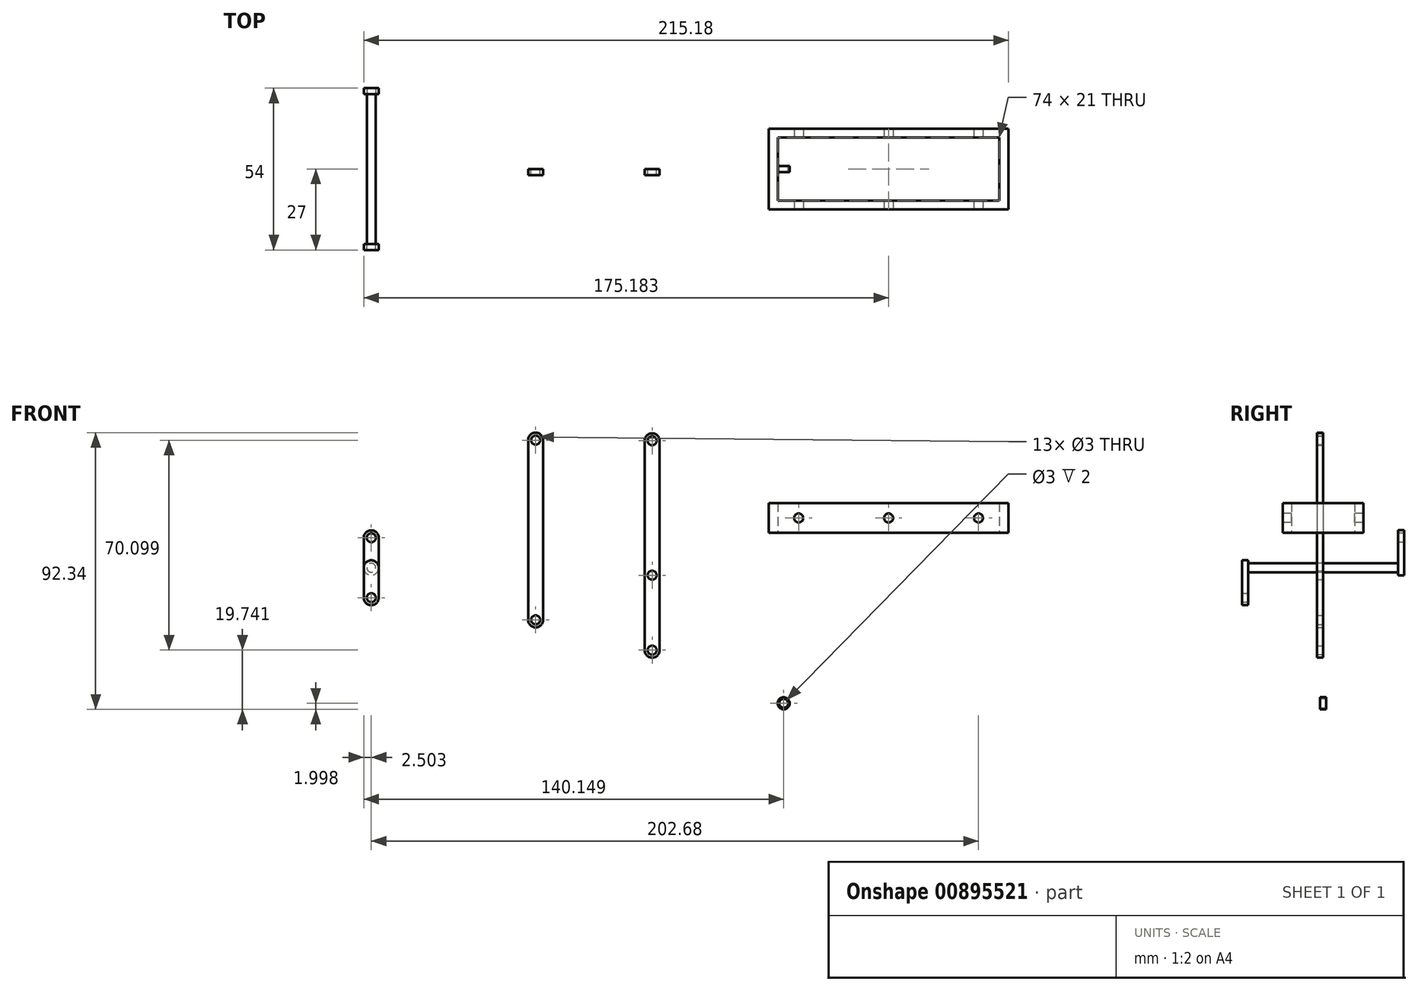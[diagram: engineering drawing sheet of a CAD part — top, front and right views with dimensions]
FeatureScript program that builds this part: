
annotation { "Feature Type Name" : "Feature", "Feature Type Description" : "" }
export const myFeature = defineFeature(function(context is Context, id is Id, definition is map)
    precondition{}
    {
        {
            var Q0;
            Q0=qCreatedBy(makeId("Front.planeOp"),FACE);
            var sketch = newSketch(context, id + "F0", { "sketchPlane" : qUnion([Q0])});
            skLineSegment(sketch, "E0.bottom", {"start": v(-57.36, 17.4) * mm, "end": v(-52.36, 17.4) * mm});
            skLineSegment(sketch, "E0.top", {"start": v(-57.36, -2.6) * mm, "end": v(-52.36, -2.6) * mm});
            skLineSegment(sketch, "E0.left", {"start": v(-57.36, 17.4) * mm, "end": v(-57.36, -2.6) * mm});
            skLineSegment(sketch, "E0.right", {"start": v(-52.36, 17.4) * mm, "end": v(-52.36, -2.6) * mm});
            skArc(sketch, "E1", {"start": v(-52.36, 17.4) * mm, "mid": v(-54.86, 19.9) * mm, "end": v(-57.36, 17.4) * mm});
            skArc(sketch, "E2", {"start": v(-57.36, -2.6) * mm, "mid": v(-54.86, -5.1) * mm, "end": v(-52.36, -2.6) * mm});
            skCircle(sketch, "E3", {"center": v(-54.86, -2.6) * mm, "radius": 1.5 * mm});
            skCircle(sketch, "E4", {"center": v(-54.86, 17.4) * mm, "radius": 1.5 * mm});
            skLineSegment(sketch, "E5", {"start": v(-57.36, 7.4) * mm, "end": v(-52.36, 7.4) * mm});
            skCircle(sketch, "E6", {"center": v(-54.86, 7.4) * mm, "radius": 2.5 * mm});
            skCircle(sketch, "E7", {"center": v(-54.86, 7.4) * mm, "radius": 1.5 * mm});
            skSolve(sketch);
        }
        {
            var Q0;
            {var subQ1=sQuery(id+"F0.wireOp",EDGE,"E5");var subQ3=sQuery(id+"F0.wireOp",EDGE,"E7");var subQ4=makeQuery(id+"F0.imprint","INTERSECT",VERTEX,{"disambiguationData":[OD(0.0)],"derivedFrom":[subQ1,subQ3]});Q0=makeQuery(id+"F0.imprint","IMPRINT",FACE,{"disambiguationData":[TD([[makeQuery(id+"F0.imprint","IMPRINT",EDGE,{"disambiguationData":[TD([[subQ4,-1.0]])],"derivedFrom":subQ3}),-1.0]])]});}
            var Q1;
            {var subQ0=sQuery(id+"F0.wireOp",EDGE,"E7");var subQ1=sQuery(id+"F0.wireOp",EDGE,"E5");var subQ2=makeQuery(id+"F0.imprint","INTERSECT",VERTEX,{"disambiguationData":[OD(0.0)],"derivedFrom":[subQ1,subQ0]});Q1=makeQuery(id+"F0.imprint","IMPRINT",FACE,{"disambiguationData":[TD([[makeQuery(id+"F0.imprint","IMPRINT",EDGE,{"disambiguationData":[TD([[subQ2,-1.0]])],"derivedFrom":subQ1}),-1.0]])]});}
            var Q2;
            {var subQ0=sQuery(id+"F0.wireOp",EDGE,"E7");var subQ1=sQuery(id+"F0.wireOp",EDGE,"E5");var subQ2=makeQuery(id+"F0.imprint","INTERSECT",VERTEX,{"disambiguationData":[OD(0.0)],"derivedFrom":[subQ1,subQ0]});Q2=makeQuery(id+"F0.imprint","IMPRINT",FACE,{"disambiguationData":[TD([[makeQuery(id+"F0.imprint","IMPRINT",EDGE,{"disambiguationData":[TD([[subQ2,-1.0]])],"derivedFrom":subQ1}),1.0]])]});}
            var Q3;
            {var subQ1=sQuery(id+"F0.wireOp",EDGE,"E5");var subQ3=sQuery(id+"F0.wireOp",EDGE,"E7");var subQ4=makeQuery(id+"F0.imprint","INTERSECT",VERTEX,{"disambiguationData":[OD(0.0)],"derivedFrom":[subQ1,subQ3]});Q3=makeQuery(id+"F0.imprint","IMPRINT",FACE,{"disambiguationData":[TD([[makeQuery(id+"F0.imprint","IMPRINT",EDGE,{"disambiguationData":[TD([[subQ4,1.0]])],"derivedFrom":subQ3}),-1.0]])]});}
            var Q4;
            {var subQ2=sQuery(id+"F0.wireOp",EDGE,"E0.bottom");var subQ10=sQuery(id+"F0.wireOp",EDGE,"E4");var subQ12=makeQuery(id+"F0.imprint","INTERSECT",VERTEX,{"disambiguationData":[OD(0.0)],"derivedFrom":[subQ2,subQ10]});Q4=makeQuery(id+"F0.imprint","IMPRINT",FACE,{"disambiguationData":[TD([[makeQuery(id+"F0.imprint","IMPRINT",EDGE,{"disambiguationData":[TD([[subQ12,-1.0]])],"derivedFrom":subQ10}),-1.0]])]});}
            var Q5;
            {var subQ0=sQuery(id+"F0.wireOp",EDGE,"E4");var subQ1=sQuery(id+"F0.wireOp",EDGE,"E0.bottom");var subQ2=makeQuery(id+"F0.imprint","INTERSECT",VERTEX,{"disambiguationData":[OD(0.0)],"derivedFrom":[subQ1,subQ0]});Q5=makeQuery(id+"F0.imprint","IMPRINT",FACE,{"disambiguationData":[TD([[makeQuery(id+"F0.imprint","IMPRINT",EDGE,{"disambiguationData":[TD([[subQ2,-1.0]])],"derivedFrom":subQ1}),-1.0]])]});}
            var Q6;
            {var subQ0=sQuery(id+"F0.wireOp",EDGE,"E4");var subQ1=sQuery(id+"F0.wireOp",EDGE,"E0.bottom");var subQ2=makeQuery(id+"F0.imprint","INTERSECT",VERTEX,{"disambiguationData":[OD(0.0)],"derivedFrom":[subQ1,subQ0]});Q6=makeQuery(id+"F0.imprint","IMPRINT",FACE,{"disambiguationData":[TD([[makeQuery(id+"F0.imprint","IMPRINT",EDGE,{"disambiguationData":[TD([[subQ2,-1.0]])],"derivedFrom":subQ1}),1.0]])]});}
            var Q7;
            {var subQ0=sQuery(id+"F0.wireOp",EDGE,"E1");Q7=makeQuery(id+"F0.imprint","IMPRINT",FACE,{"disambiguationData":[TD([[makeQuery(id+"F0.imprint","IMPRINT",EDGE,{"derivedFrom":subQ0}),1.0]])]});}
            extrude(context, id + "F1", {"entities" : qUnion([Q0, Q1, Q2, Q3, Q4, Q5, Q6, Q7]), "oppositeDirection" : true, "depth" : 27 * mm, "offsetDistance" : 25 * mm});
        }
        {
            var Q0;
            {var subQ1=sQuery(id+"F0.wireOp",EDGE,"E5");var subQ3=sQuery(id+"F0.wireOp",EDGE,"E7");var subQ4=makeQuery(id+"F0.imprint","INTERSECT",VERTEX,{"disambiguationData":[OD(0.0)],"derivedFrom":[subQ1,subQ3]});Q0=makeQuery(id+"F0.imprint","IMPRINT",FACE,{"disambiguationData":[TD([[makeQuery(id+"F0.imprint","IMPRINT",EDGE,{"disambiguationData":[TD([[subQ4,1.0]])],"derivedFrom":subQ3}),-1.0]])]});}
            var Q1;
            {var subQ0=sQuery(id+"F0.wireOp",EDGE,"E7");var subQ1=sQuery(id+"F0.wireOp",EDGE,"E5");var subQ2=makeQuery(id+"F0.imprint","INTERSECT",VERTEX,{"disambiguationData":[OD(0.0)],"derivedFrom":[subQ1,subQ0]});Q1=makeQuery(id+"F0.imprint","IMPRINT",FACE,{"disambiguationData":[TD([[makeQuery(id+"F0.imprint","IMPRINT",EDGE,{"disambiguationData":[TD([[subQ2,-1.0]])],"derivedFrom":subQ1}),1.0]])]});}
            var Q2;
            {var subQ0=sQuery(id+"F0.wireOp",EDGE,"E7");var subQ1=sQuery(id+"F0.wireOp",EDGE,"E5");var subQ2=makeQuery(id+"F0.imprint","INTERSECT",VERTEX,{"disambiguationData":[OD(0.0)],"derivedFrom":[subQ1,subQ0]});Q2=makeQuery(id+"F0.imprint","IMPRINT",FACE,{"disambiguationData":[TD([[makeQuery(id+"F0.imprint","IMPRINT",EDGE,{"disambiguationData":[TD([[subQ2,-1.0]])],"derivedFrom":subQ1}),-1.0]])]});}
            var Q3;
            {var subQ1=sQuery(id+"F0.wireOp",EDGE,"E5");var subQ3=sQuery(id+"F0.wireOp",EDGE,"E7");var subQ4=makeQuery(id+"F0.imprint","INTERSECT",VERTEX,{"disambiguationData":[OD(0.0)],"derivedFrom":[subQ1,subQ3]});Q3=makeQuery(id+"F0.imprint","IMPRINT",FACE,{"disambiguationData":[TD([[makeQuery(id+"F0.imprint","IMPRINT",EDGE,{"disambiguationData":[TD([[subQ4,-1.0]])],"derivedFrom":subQ3}),-1.0]])]});}
            var Q4;
            {var subQ2=sQuery(id+"F0.wireOp",EDGE,"E0.top");var subQ10=sQuery(id+"F0.wireOp",EDGE,"E3");var subQ12=makeQuery(id+"F0.imprint","INTERSECT",VERTEX,{"disambiguationData":[OD(0.0)],"derivedFrom":[subQ2,subQ10]});Q4=makeQuery(id+"F0.imprint","IMPRINT",FACE,{"disambiguationData":[TD([[makeQuery(id+"F0.imprint","IMPRINT",EDGE,{"disambiguationData":[TD([[subQ12,1.0]])],"derivedFrom":subQ10}),-1.0]])]});}
            var Q5;
            {var subQ0=sQuery(id+"F0.wireOp",EDGE,"E2");Q5=makeQuery(id+"F0.imprint","IMPRINT",FACE,{"disambiguationData":[TD([[makeQuery(id+"F0.imprint","IMPRINT",EDGE,{"derivedFrom":subQ0}),1.0]])]});}
            extrude(context, id + "F2", {"entities" : qUnion([Q0, Q1, Q2, Q3, Q4, Q5]), "operationType" : NewBodyOperationType.ADD, "depth" : 27 * mm, "offsetDistance" : 25 * mm});
        }
        {
            var Q0;
            {var subQ0=sQuery(id+"F0.wireOp",EDGE,"E4");var subQ1=sQuery(id+"F0.wireOp",EDGE,"E0.bottom");var subQ2=makeQuery(id+"F0.imprint","INTERSECT",VERTEX,{"disambiguationData":[OD(0.0)],"derivedFrom":[subQ1,subQ0]});Q0=makeQuery(id+"F0.imprint","IMPRINT",FACE,{"disambiguationData":[TD([[makeQuery(id+"F0.imprint","IMPRINT",EDGE,{"disambiguationData":[TD([[subQ2,-1.0]])],"derivedFrom":subQ1}),1.0]])]});}
            var Q1;
            {var subQ0=sQuery(id+"F0.wireOp",EDGE,"E4");var subQ1=sQuery(id+"F0.wireOp",EDGE,"E0.bottom");var subQ2=makeQuery(id+"F0.imprint","INTERSECT",VERTEX,{"disambiguationData":[OD(0.0)],"derivedFrom":[subQ1,subQ0]});Q1=makeQuery(id+"F0.imprint","IMPRINT",FACE,{"disambiguationData":[TD([[makeQuery(id+"F0.imprint","IMPRINT",EDGE,{"disambiguationData":[TD([[subQ2,-1.0]])],"derivedFrom":subQ1}),-1.0]])]});}
            extrude(context, id + "F3", {"entities" : qUnion([Q0, Q1]), "operationType" : NewBodyOperationType.REMOVE, "oppositeDirection" : true, "depth" : 27 * mm, "offsetDistance" : 25 * mm});
        }
        {
            var Q0;
            Q0=qSketchRegion(id+"F0",true);
            extrude(context, id + "F4", {"entities" : qUnion([Q0]), "operationType" : NewBodyOperationType.REMOVE, "oppositeDirection" : true, "depth" : 25 * mm, "offsetDistance" : 25 * mm});
        }
        {
            var Q0;
            {var subQ1=sQuery(id+"F0.wireOp",EDGE,"E5");var subQ3=sQuery(id+"F0.wireOp",EDGE,"E7");var subQ4=makeQuery(id+"F0.imprint","INTERSECT",VERTEX,{"disambiguationData":[OD(0.0)],"derivedFrom":[subQ1,subQ3]});Q0=makeQuery(id+"F0.imprint","IMPRINT",FACE,{"disambiguationData":[TD([[makeQuery(id+"F0.imprint","IMPRINT",EDGE,{"disambiguationData":[TD([[subQ4,-1.0]])],"derivedFrom":subQ3}),-1.0]])]});}
            var Q1;
            {var subQ2=sQuery(id+"F0.wireOp",EDGE,"E0.top");var subQ10=sQuery(id+"F0.wireOp",EDGE,"E3");var subQ12=makeQuery(id+"F0.imprint","INTERSECT",VERTEX,{"disambiguationData":[OD(0.0)],"derivedFrom":[subQ2,subQ10]});Q1=makeQuery(id+"F0.imprint","IMPRINT",FACE,{"disambiguationData":[TD([[makeQuery(id+"F0.imprint","IMPRINT",EDGE,{"disambiguationData":[TD([[subQ12,1.0]])],"derivedFrom":subQ10}),-1.0]])]});}
            var Q2;
            {var subQ0=sQuery(id+"F0.wireOp",EDGE,"E2");Q2=makeQuery(id+"F0.imprint","IMPRINT",FACE,{"disambiguationData":[TD([[makeQuery(id+"F0.imprint","IMPRINT",EDGE,{"derivedFrom":subQ0}),1.0]])]});}
            extrude(context, id + "F5", {"entities" : qUnion([Q0, Q1, Q2]), "operationType" : NewBodyOperationType.REMOVE, "depth" : 25 * mm, "offsetDistance" : 25 * mm});
        }
        {
            var Q0;
            {var subQ1=sQuery(id+"F0.wireOp",EDGE,"E5");var subQ3=sQuery(id+"F0.wireOp",EDGE,"E7");var subQ4=makeQuery(id+"F0.imprint","INTERSECT",VERTEX,{"disambiguationData":[OD(0.0)],"derivedFrom":[subQ1,subQ3]});Q0=makeQuery(id+"F0.imprint","IMPRINT",FACE,{"disambiguationData":[TD([[makeQuery(id+"F0.imprint","IMPRINT",EDGE,{"disambiguationData":[TD([[subQ4,1.0]])],"derivedFrom":subQ3}),-1.0]])]});}
            extrude(context, id + "F6", {"entities" : qUnion([Q0]), "operationType" : NewBodyOperationType.REMOVE, "depth" : 25 * mm, "offsetDistance" : 25 * mm});
        }
        {
            var Q0;
            Q0=qCreatedBy(makeId("Front.planeOp"),FACE);
            var sketch = newSketch(context, id + "F7", { "sketchPlane" : qUnion([Q0])});
            skLineSegment(sketch, "E8.bottom", {"start": v(-2.5, 50) * mm, "end": v(2.5, 50) * mm});
            skLineSegment(sketch, "E8.top", {"start": v(-2.5, -10) * mm, "end": v(2.5, -10) * mm});
            skLineSegment(sketch, "E8.left", {"start": v(-2.5, 50) * mm, "end": v(-2.5, -10) * mm});
            skLineSegment(sketch, "E8.right", {"start": v(2.5, 50) * mm, "end": v(2.5, -10) * mm});
            skArc(sketch, "E9", {"start": v(2.5, 50) * mm, "mid": v(0, 52.5) * mm, "end": v(-2.5, 50) * mm});
            skArc(sketch, "E10", {"start": v(-2.5, -10) * mm, "mid": v(0, -12.5) * mm, "end": v(2.5, -10) * mm});
            skCircle(sketch, "E11", {"center": v(0, -10) * mm, "radius": 1.5 * mm});
            skCircle(sketch, "E12", {"center": v(0, 50) * mm, "radius": 1.5 * mm});
            skSolve(sketch);
        }
        {
            var Q0;
            {var subQ1=sQuery(id+"F7.wireOp",EDGE,"E8.left");Q0=makeQuery(id+"F7.imprint","IMPRINT",FACE,{"disambiguationData":[TD([[makeQuery(id+"F7.imprint","IMPRINT",EDGE,{"derivedFrom":subQ1}),1.0]])]});}
            var Q1;
            {var subQ0=sQuery(id+"F7.wireOp",EDGE,"E9");Q1=makeQuery(id+"F7.imprint","IMPRINT",FACE,{"disambiguationData":[TD([[makeQuery(id+"F7.imprint","IMPRINT",EDGE,{"derivedFrom":subQ0}),1.0]])]});}
            var Q2;
            {var subQ0=sQuery(id+"F7.wireOp",EDGE,"E10");Q2=makeQuery(id+"F7.imprint","IMPRINT",FACE,{"disambiguationData":[TD([[makeQuery(id+"F7.imprint","IMPRINT",EDGE,{"derivedFrom":subQ0}),1.0]])]});}
            extrude(context, id + "F8", {"entities" : qUnion([Q0, Q1, Q2]), "depth" : 2 * mm, "offsetDistance" : 25 * mm});
        }
        {
            var Q0;
            Q0=qCreatedBy(makeId("Front.planeOp"),FACE);
            var sketch = newSketch(context, id + "F9", { "sketchPlane" : qUnion([Q0])});
            skLineSegment(sketch, "E13.bottom", {"start": v(36.4, 49.8) * mm, "end": v(41.4, 49.8) * mm});
            skLineSegment(sketch, "E13.top", {"start": v(36.4, -20.1) * mm, "end": v(41.4, -20.1) * mm});
            skLineSegment(sketch, "E13.left", {"start": v(36.4, 49.8) * mm, "end": v(36.4, -20.1) * mm});
            skLineSegment(sketch, "E13.right", {"start": v(41.4, 49.8) * mm, "end": v(41.4, -20.1) * mm});
            skArc(sketch, "E14", {"start": v(36.4, -20.1) * mm, "mid": v(38.9, -22.6) * mm, "end": v(41.4, -20.1) * mm});
            skArc(sketch, "E15", {"start": v(41.4, 49.8) * mm, "mid": v(38.9, 52.3) * mm, "end": v(36.4, 49.8) * mm});
            skLineSegment(sketch, "E16.0", {"start": v(36.4, 4.9) * mm, "end": v(41.4, 4.9) * mm});
            skCircle(sketch, "E17", {"center": v(38.9, 4.9) * mm, "radius": 1.5 * mm});
            skCircle(sketch, "E18", {"center": v(38.9, 49.8) * mm, "radius": 1.5 * mm});
            skCircle(sketch, "E19", {"center": v(38.9, -20.1) * mm, "radius": 1.5 * mm});
            skSolve(sketch);
        }
        {
            var Q0;
            {var subQ4=sQuery(id+"F9.wireOp",EDGE,"E16.0");var subQ6=sQuery(id+"F9.wireOp",EDGE,"E13.left");var subQ8=makeQuery(id+"F9.imprint","INTERSECT",VERTEX,{"derivedFrom":[subQ6,subQ4]});Q0=makeQuery(id+"F9.imprint","IMPRINT",FACE,{"disambiguationData":[TD([[makeQuery(id+"F9.imprint","IMPRINT",EDGE,{"disambiguationData":[TD([[subQ8,-1.0]])],"derivedFrom":subQ4}),1.0]])]});}
            var Q1;
            {var subQ4=sQuery(id+"F9.wireOp",EDGE,"E16.0");var subQ6=sQuery(id+"F9.wireOp",EDGE,"E13.left");var subQ8=makeQuery(id+"F9.imprint","INTERSECT",VERTEX,{"derivedFrom":[subQ6,subQ4]});Q1=makeQuery(id+"F9.imprint","IMPRINT",FACE,{"disambiguationData":[TD([[makeQuery(id+"F9.imprint","IMPRINT",EDGE,{"disambiguationData":[TD([[subQ8,-1.0]])],"derivedFrom":subQ4}),-1.0]])]});}
            var Q2;
            {var subQ0=sQuery(id+"F9.wireOp",EDGE,"E14");Q2=makeQuery(id+"F9.imprint","IMPRINT",FACE,{"disambiguationData":[TD([[makeQuery(id+"F9.imprint","IMPRINT",EDGE,{"derivedFrom":subQ0}),1.0]])]});}
            var Q3;
            {var subQ0=sQuery(id+"F9.wireOp",EDGE,"E15");Q3=makeQuery(id+"F9.imprint","IMPRINT",FACE,{"disambiguationData":[TD([[makeQuery(id+"F9.imprint","IMPRINT",EDGE,{"derivedFrom":subQ0}),1.0]])]});}
            extrude(context, id + "F10", {"entities" : qUnion([Q0, Q1, Q2, Q3]), "depth" : 2 * mm, "offsetDistance" : 25 * mm});
        }
        {
            var Q0;
            Q0=qCreatedBy(makeId("Front.planeOp"),FACE);
            var sketch = newSketch(context, id + "F11", { "sketchPlane" : qUnion([Q0])});
            skLineSegment(sketch, "E20.bottom", {"start": v(77.82, 29.02) * mm, "end": v(157.82, 29.02) * mm});
            skLineSegment(sketch, "E20.top", {"start": v(77.82, 19.02) * mm, "end": v(157.82, 19.02) * mm});
            skLineSegment(sketch, "E20.left", {"start": v(77.82, 29.02) * mm, "end": v(77.82, 19.02) * mm});
            skLineSegment(sketch, "E20.right", {"start": v(157.82, 29.02) * mm, "end": v(157.82, 19.02) * mm});
            skCircle(sketch, "E21", {"center": v(85.37, 24.02) * mm, "radius": 1.5 * mm});
            skCircle(sketch, "E22", {"center": v(115.37, 24.02) * mm, "radius": 1.5 * mm});
            skCircle(sketch, "E23", {"center": v(145.37, 24.02) * mm, "radius": 1.5 * mm});
            skSolve(sketch);
        }
        {
            var Q0;
            {var subQ5=sQuery(id+"F11.wireOp",EDGE,"E20.bottom");Q0=makeQuery(id+"F11.imprint","IMPRINT",FACE,{"disambiguationData":[TD([[makeQuery(id+"F11.imprint","IMPRINT",EDGE,{"derivedFrom":subQ5}),-1.0]])]});}
            var Q1;
            {var subQ8=sQuery(id+"F11.wireOp",EDGE,"E20.top");Q1=makeQuery(id+"F11.imprint","IMPRINT",FACE,{"disambiguationData":[TD([[makeQuery(id+"F11.imprint","IMPRINT",EDGE,{"derivedFrom":subQ8}),1.0]])]});}
            var Q2;
            Q2=makeQuery(id+"F11.imprint","IMPRINT",FACE,{"disambiguationData":[TD([[makeQuery(id+"F11.imprint","IMPRINT",EDGE,{"derivedFrom":sQuery(id+"F11.wireOp",EDGE,"E22")}),1.0]])]});
            var Q3;
            Q3=makeQuery(id+"F11.imprint","IMPRINT",FACE,{"disambiguationData":[TD([[makeQuery(id+"F11.imprint","IMPRINT",EDGE,{"derivedFrom":sQuery(id+"F11.wireOp",EDGE,"E23")}),1.0]])]});
            var Q4;
            Q4=makeQuery(id+"F11.imprint","IMPRINT",FACE,{"disambiguationData":[TD([[makeQuery(id+"F11.imprint","IMPRINT",EDGE,{"derivedFrom":sQuery(id+"F11.wireOp",EDGE,"E21")}),1.0]])]});
            extrude(context, id + "F12", {"entities" : qUnion([Q0, Q1, Q2, Q3, Q4]), "endBound" : BoundingType.SYMMETRIC, "depth" : 27 * mm, "offsetDistance" : 25 * mm});
        }
        {
            var Q0;
            Q0=makeQuery(id+"F12.opExtrude","SWEPT_FACE",FACE,{"disambiguationData":[OSD([sQuery(id+"F11.wireOp",EDGE,"E20.bottom")])]});
            var Q1;
            Q1=makeQuery(id+"F12.opExtrude","SWEPT_FACE",FACE,{"disambiguationData":[OSD([sQuery(id+"F11.wireOp",EDGE,"E20.top")])]});
            shell(context, id + "F13", {"entities" : qUnion([Q0, Q1]), "thickness" : 3 * mm});
        }
        {
            var Q0;
            Q0=makeQuery(id+"F12.opExtrude","CAP_FACE",FACE,{"disambiguationData":[OSD([sQuery(id+"F11.wireOp",EDGE,"E20.bottom"),sQuery(id+"F11.wireOp",EDGE,"E20.top"),sQuery(id+"F11.wireOp",EDGE,"E20.left"),sQuery(id+"F11.wireOp",EDGE,"E20.right")])],"isStart":false});
            var sketch = newSketch(context, id + "F14", { "sketchPlane" : qUnion([Q0])});
            skCircle(sketch, "E24", {"center": v(87.82, 24.02) * mm, "radius": 1.5 * mm});
            skCircle(sketch, "E25", {"center": v(117.82, 24.02) * mm, "radius": 1.5 * mm});
            skCircle(sketch, "E26", {"center": v(147.82, 24.02) * mm, "radius": 1.5 * mm});
            skLineSegment(sketch, "E27", {"start": v(77.82, 24.02) * mm, "end": v(157.82, 24.02) * mm});
            skSolve(sketch);
        }
        {
            var Q0;
            {var subQ0=sQuery(id+"F14.wireOp",EDGE,"E27");var subQ1=sQuery(id+"F14.wireOp",EDGE,"E26");var subQ2=makeQuery(id+"F14.imprint","INTERSECT",VERTEX,{"disambiguationData":[OD(0.0)],"derivedFrom":[subQ1,subQ0]});Q0=makeQuery(id+"F14.imprint","IMPRINT",FACE,{"disambiguationData":[TD([[makeQuery(id+"F14.imprint","IMPRINT",EDGE,{"disambiguationData":[TD([[subQ2,1.0]])],"derivedFrom":subQ1}),1.0]])]});}
            var Q1;
            {var subQ0=sQuery(id+"F14.wireOp",EDGE,"E27");var subQ1=sQuery(id+"F14.wireOp",EDGE,"E26");var subQ2=makeQuery(id+"F14.imprint","INTERSECT",VERTEX,{"disambiguationData":[OD(0.0)],"derivedFrom":[subQ1,subQ0]});Q1=makeQuery(id+"F14.imprint","IMPRINT",FACE,{"disambiguationData":[TD([[makeQuery(id+"F14.imprint","IMPRINT",EDGE,{"disambiguationData":[TD([[subQ2,-1.0]])],"derivedFrom":subQ1}),1.0]])]});}
            var Q2;
            {var subQ0=sQuery(id+"F14.wireOp",EDGE,"E27");var subQ1=sQuery(id+"F14.wireOp",EDGE,"E25");var subQ2=makeQuery(id+"F14.imprint","INTERSECT",VERTEX,{"disambiguationData":[OD(0.0)],"derivedFrom":[subQ1,subQ0]});Q2=makeQuery(id+"F14.imprint","IMPRINT",FACE,{"disambiguationData":[TD([[makeQuery(id+"F14.imprint","IMPRINT",EDGE,{"disambiguationData":[TD([[subQ2,1.0]])],"derivedFrom":subQ1}),1.0]])]});}
            var Q3;
            {var subQ0=sQuery(id+"F14.wireOp",EDGE,"E27");var subQ1=sQuery(id+"F14.wireOp",EDGE,"E25");var subQ2=makeQuery(id+"F14.imprint","INTERSECT",VERTEX,{"disambiguationData":[OD(0.0)],"derivedFrom":[subQ1,subQ0]});Q3=makeQuery(id+"F14.imprint","IMPRINT",FACE,{"disambiguationData":[TD([[makeQuery(id+"F14.imprint","IMPRINT",EDGE,{"disambiguationData":[TD([[subQ2,-1.0]])],"derivedFrom":subQ1}),1.0]])]});}
            var Q4;
            {var subQ0=sQuery(id+"F14.wireOp",EDGE,"E27");var subQ1=sQuery(id+"F14.wireOp",EDGE,"E24");var subQ2=makeQuery(id+"F14.imprint","INTERSECT",VERTEX,{"disambiguationData":[OD(0.0)],"derivedFrom":[subQ1,subQ0]});Q4=makeQuery(id+"F14.imprint","IMPRINT",FACE,{"disambiguationData":[TD([[makeQuery(id+"F14.imprint","IMPRINT",EDGE,{"disambiguationData":[TD([[subQ2,1.0]])],"derivedFrom":subQ1}),1.0]])]});}
            var Q5;
            {var subQ0=sQuery(id+"F14.wireOp",EDGE,"E27");var subQ1=sQuery(id+"F14.wireOp",EDGE,"E24");var subQ2=makeQuery(id+"F14.imprint","INTERSECT",VERTEX,{"disambiguationData":[OD(0.0)],"derivedFrom":[subQ1,subQ0]});Q5=makeQuery(id+"F14.imprint","IMPRINT",FACE,{"disambiguationData":[TD([[makeQuery(id+"F14.imprint","IMPRINT",EDGE,{"disambiguationData":[TD([[subQ2,-1.0]])],"derivedFrom":subQ1}),1.0]])]});}
            extrude(context, id + "F15", {"entities" : qUnion([Q0, Q1, Q2, Q3, Q4, Q5]), "operationType" : NewBodyOperationType.REMOVE, "endBound" : BoundingType.THROUGH_ALL, "oppositeDirection" : true, "depth" : 25 * mm, "offsetDistance" : 25 * mm});
        }
        {
            var Q0;
            Q0=qCreatedBy(makeId("Front.planeOp"),FACE);
            var sketch = newSketch(context, id + "F16", { "sketchPlane" : qUnion([Q0])});
            skCircle(sketch, "E28", {"center": v(82.79, -37.84) * mm, "radius": 2 * mm});
            skCircle(sketch, "E29", {"center": v(82.79, -37.84) * mm, "radius": 1.5 * mm});
            skSolve(sketch);
        }
        {
            var Q0;
            Q0=makeQuery(id+"F16.imprint","IMPRINT",FACE,{"disambiguationData":[TD([[makeQuery(id+"F16.imprint","IMPRINT",EDGE,{"derivedFrom":sQuery(id+"F16.wireOp",EDGE,"E28")}),1.0]])]});
            extrude(context, id + "F17", {"entities" : qUnion([Q0]), "endBound" : BoundingType.SYMMETRIC, "depth" : 2 * mm, "offsetDistance" : 25 * mm});
        }
    });
